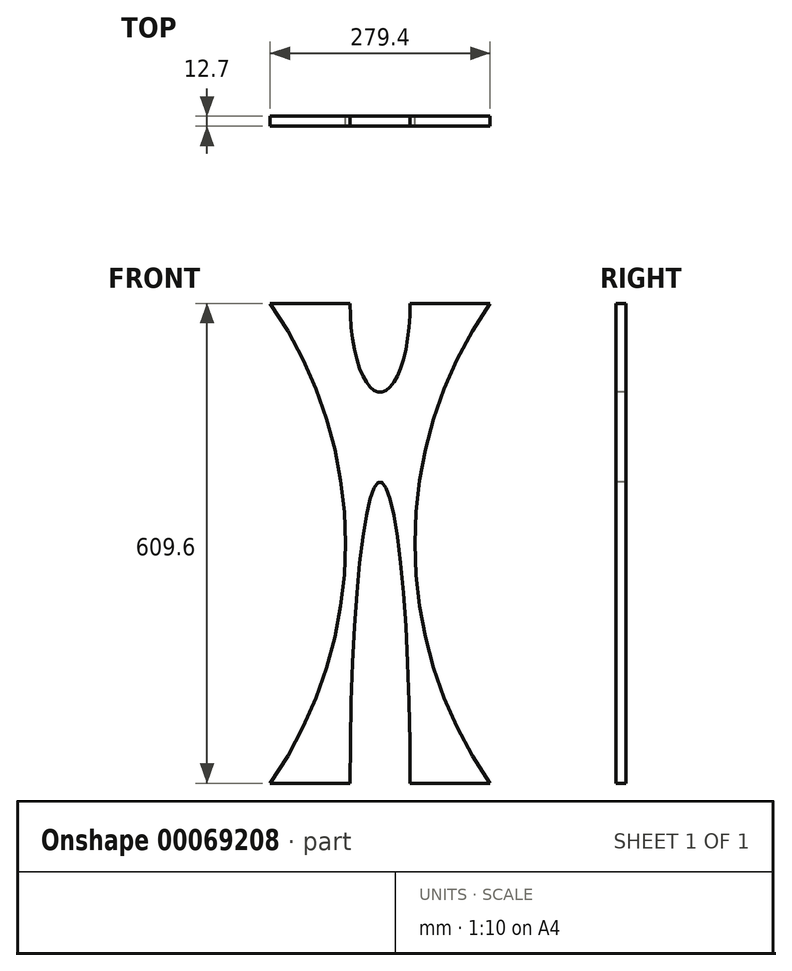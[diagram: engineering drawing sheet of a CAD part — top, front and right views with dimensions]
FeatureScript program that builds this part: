
annotation { "Feature Type Name" : "Feature", "Feature Type Description" : "" }
export const myFeature = defineFeature(function(context is Context, id is Id, definition is map)
    precondition{}
    {
        {
            var Q0;
            Q0=qCreatedBy(makeId("Front.planeOp"),FACE);
            var sketch = newSketch(context, id + "F0", { "sketchPlane" : qUnion([Q0])});
            skLineSegment(sketch, "E0", {"start": v(0, 0) * mm, "end": v(101.6, 0) * mm});
            skLineSegment(sketch, "E1", {"start": v(101.6, 609.6) * mm, "end": v(0, 609.6) * mm});
            skLineSegment(sketch, "E2", {"start": v(0, 0) * mm, "end": v(0, 704.65) * mm, "construction": true});
            skLineSegment(sketch, "E3", {"start": v(-38.1, 0) * mm, "end": v(-38.1, 704.65) * mm, "construction": true});
            skLineSegment(sketch, "E4", {"start": v(-135.6, 355.6) * mm, "end": v(135.5, 355.6) * mm, "construction": true});
            skArc(sketch, "E5", {"start": v(101.6, 609.6) * mm, "mid": v(5.94, 304.8) * mm, "end": v(101.6, 0) * mm});
            skEllipticalArc(sketch, "E6", {});
            skEllipticalArc(sketch, "E7", {});
            skLineSegment(sketch, "E8.MirrorCS", {"start": v(-177.8, 609.6) * mm, "end": v(-76.2, 609.6) * mm});
            skLineSegment(sketch, "E9.MirrorCS", {"start": v(-76.2, 0) * mm, "end": v(-177.8, 0) * mm});
            skArc(sketch, "E10.MirrorCS", {"start": v(-177.8, 609.6) * mm, "mid": v(-82.14, 304.8) * mm, "end": v(-177.8, 0) * mm});
            skEllipticalArc(sketch, "E11.MirrorCS", {});
            skEllipticalArc(sketch, "E12.MirrorCS", {});
            const initialGuessF0  = {"E6": [-0.0381, 0, 1, 0, 0.0381, 0.3830003180913211, 6.283185307179586, 1.5707963267948966], "E7": [-0.0381, 0.6096, 1, 0, 0.0381, 0.1128433488107344, 4.71238898038469, 6.283185307179586], "E11.MirrorCS": [-0.0381, 0.6096, -1, 0, 0.0381, 0.1128433488107344, 6.283185307179586, 1.5707963267948966], "E12.MirrorCS": [-0.0381, 0, -1, 0, 0.0381, 0.3830003180913211, 4.71238898038469, 6.283185307179586]};
            skSetInitialGuess(sketch, initialGuessF0);
            skSolve(sketch);
        }
        {
            var Q0;
            Q0 = qSketchRegion(id + "F0", true);
            extrude(context, id + "F1", {"entities" : qUnion([Q0]), "depth" : 12.7 * mm});
        }
    });
